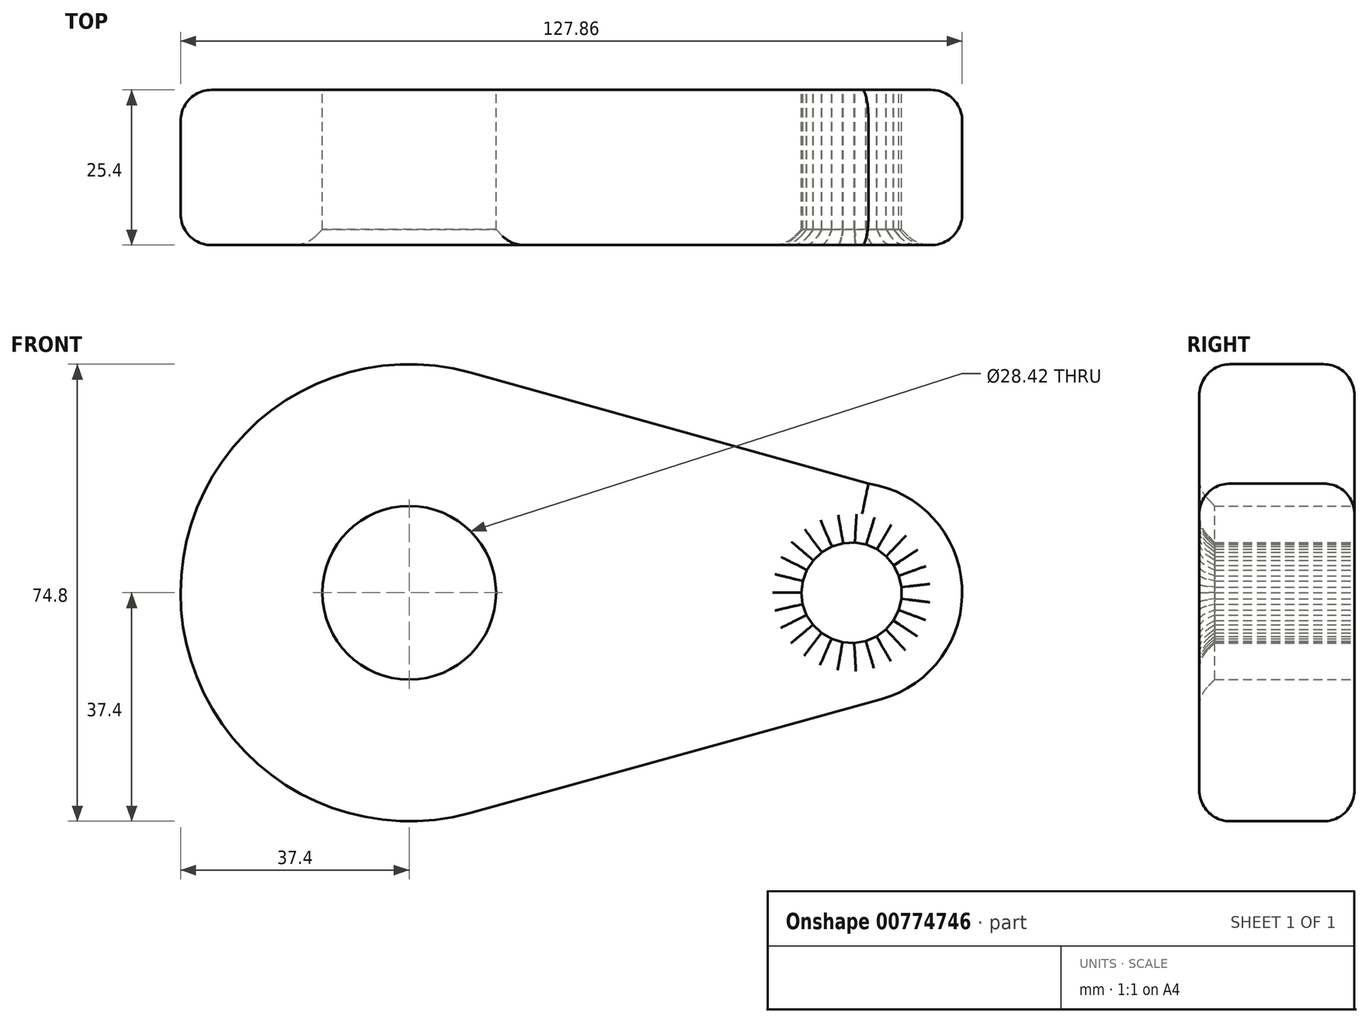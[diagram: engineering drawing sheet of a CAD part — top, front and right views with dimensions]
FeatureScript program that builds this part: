
annotation { "Feature Type Name" : "Feature", "Feature Type Description" : "" }
export const myFeature = defineFeature(function(context is Context, id is Id, definition is map)
    precondition{}
    {
        {
            var Q0;
            Q0=qCreatedBy(makeId("Front.planeOp"),FACE);
            var sketch = newSketch(context, id + "F0", { "sketchPlane" : qUnion([Q0])});
            skCircle(sketch, "E0", {"center": v(0, 0) * mm, "radius": 37.4 * mm});
            skCircle(sketch, "E1", {"center": v(0, 0) * mm, "radius": 14.2 * mm});
            skCircle(sketch, "E2", {"center": v(72.37, 0) * mm, "radius": 18.1 * mm});
            skCircle(sketch, "E3.cCircle", {"center": v(72.37, 0) * mm, "radius": 8.17 * mm, "construction": true});
            skLineSegment(sketch, "E3.0", {"start": v(67.49, 6.62) * mm, "end": v(69.15, 7.57) * mm});
            skLineSegment(sketch, "E3.1", {"start": v(69.15, 7.57) * mm, "end": v(70.98, 8.1) * mm});
            skLineSegment(sketch, "E3.2", {"start": v(70.98, 8.1) * mm, "end": v(72.89, 8.21) * mm});
            skLineSegment(sketch, "E3.3", {"start": v(72.89, 8.21) * mm, "end": v(74.77, 7.87) * mm});
            skLineSegment(sketch, "E3.4", {"start": v(74.77, 7.87) * mm, "end": v(76.52, 7.1) * mm});
            skLineSegment(sketch, "E3.5", {"start": v(76.52, 7.1) * mm, "end": v(78.04, 5.96) * mm});
            skLineSegment(sketch, "E3.6", {"start": v(78.04, 5.96) * mm, "end": v(79.26, 4.5) * mm});
            skLineSegment(sketch, "E3.7", {"start": v(79.26, 4.5) * mm, "end": v(80.11, 2.78) * mm});
            skLineSegment(sketch, "E3.8", {"start": v(80.11, 2.78) * mm, "end": v(80.55, 0.92) * mm});
            skLineSegment(sketch, "E3.9", {"start": v(80.55, 0.92) * mm, "end": v(80.54, -1) * mm});
            skLineSegment(sketch, "E3.10", {"start": v(80.54, -1) * mm, "end": v(80.09, -2.85) * mm});
            skLineSegment(sketch, "E3.11", {"start": v(80.09, -2.85) * mm, "end": v(79.22, -4.55) * mm});
            skLineSegment(sketch, "E3.12", {"start": v(79.22, -4.55) * mm, "end": v(78, -6) * mm});
            skLineSegment(sketch, "E3.13", {"start": v(78, -6) * mm, "end": v(76.45, -7.14) * mm});
            skLineSegment(sketch, "E3.14", {"start": v(76.45, -7.14) * mm, "end": v(74.7, -7.9) * mm});
            skLineSegment(sketch, "E3.15", {"start": v(74.7, -7.9) * mm, "end": v(72.81, -8.22) * mm});
            skLineSegment(sketch, "E3.16", {"start": v(72.81, -8.22) * mm, "end": v(70.9, -8.1) * mm});
            skLineSegment(sketch, "E3.17", {"start": v(70.9, -8.1) * mm, "end": v(69.08, -7.54) * mm});
            skLineSegment(sketch, "E3.18", {"start": v(69.08, -7.54) * mm, "end": v(67.43, -6.58) * mm});
            skLineSegment(sketch, "E3.19", {"start": v(67.43, -6.58) * mm, "end": v(66.04, -5.26) * mm});
            skLineSegment(sketch, "E3.20", {"start": v(66.04, -5.26) * mm, "end": v(65, -3.66) * mm});
            skLineSegment(sketch, "E3.21", {"start": v(65, -3.66) * mm, "end": v(64.36, -1.86) * mm});
            skLineSegment(sketch, "E3.22", {"start": v(64.36, -1.86) * mm, "end": v(64.14, 0.04) * mm});
            skLineSegment(sketch, "E3.23", {"start": v(64.14, 0.04) * mm, "end": v(64.37, 1.93) * mm});
            skLineSegment(sketch, "E3.24", {"start": v(64.37, 1.93) * mm, "end": v(65.03, 3.73) * mm});
            skLineSegment(sketch, "E3.25", {"start": v(65.03, 3.73) * mm, "end": v(66.1, 5.32) * mm});
            skLineSegment(sketch, "E3.26", {"start": v(66.1, 5.32) * mm, "end": v(67.49, 6.62) * mm});
            skPoint(sketch, "E3.0.midPoint", {"position": v(68.32, 7.1) * mm});
            skLineSegment(sketch, "E4", {"start": v(10.04, 36.02) * mm, "end": v(75.13, 17.88) * mm});
            skLineSegment(sketch, "E5", {"start": v(77.2, -17.44) * mm, "end": v(9.98, -36.04) * mm});
            skSolve(sketch);
        }
        {
            var Q0;
            Q0 = qSketchRegion(id + "F0", true);
            extrude(context, id + "F1", {"entities" : qUnion([Q0]), "depth" : 25.4 * mm, "offsetDistance" : 25.4 * mm});
        }
        {
            var Q0;
            Q0=makeQuery(id+"F1.opExtrude","CAP_EDGE",EDGE,{"disambiguationData":[OSD([sQuery(id+"F0.wireOp",EDGE,"E1")])],"isStart":false});
            var Q1;
            Q1=makeQuery(id+"F1.opExtrude","CAP_EDGE",EDGE,{"disambiguationData":[OSD([sQuery(id+"F0.wireOp",EDGE,"E3.4")])],"isStart":false});
            var Q2;
            Q2=makeQuery(id+"F1.opExtrude","CAP_EDGE",EDGE,{"disambiguationData":[OSD([sQuery(id+"F0.wireOp",EDGE,"E3.12")])],"isStart":false});
            var Q3;
            Q3=makeQuery(id+"F1.opExtrude","CAP_EDGE",EDGE,{"disambiguationData":[OSD([sQuery(id+"F0.wireOp",EDGE,"E3.20")])],"isStart":false});
            var Q4;
            Q4=makeQuery(id+"F1.opExtrude","CAP_EDGE",EDGE,{"disambiguationData":[OSD([sQuery(id+"F0.wireOp",EDGE,"E3.5")])],"isStart":false});
            var Q5;
            Q5=makeQuery(id+"F1.opExtrude","CAP_EDGE",EDGE,{"disambiguationData":[OSD([sQuery(id+"F0.wireOp",EDGE,"E3.13")])],"isStart":false});
            var Q6;
            Q6=makeQuery(id+"F1.opExtrude","CAP_EDGE",EDGE,{"disambiguationData":[OSD([sQuery(id+"F0.wireOp",EDGE,"E3.21")])],"isStart":false});
            var Q7;
            Q7=makeQuery(id+"F1.opExtrude","CAP_EDGE",EDGE,{"disambiguationData":[OSD([sQuery(id+"F0.wireOp",EDGE,"E3.6")])],"isStart":false});
            var Q8;
            Q8=makeQuery(id+"F1.opExtrude","CAP_EDGE",EDGE,{"disambiguationData":[OSD([sQuery(id+"F0.wireOp",EDGE,"E3.14")])],"isStart":false});
            var Q9;
            Q9=makeQuery(id+"F1.opExtrude","CAP_EDGE",EDGE,{"disambiguationData":[OSD([sQuery(id+"F0.wireOp",EDGE,"E3.22")])],"isStart":false});
            var Q10;
            Q10=makeQuery(id+"F1.opExtrude","CAP_EDGE",EDGE,{"disambiguationData":[OSD([sQuery(id+"F0.wireOp",EDGE,"E3.7")])],"isStart":false});
            var Q11;
            Q11=makeQuery(id+"F1.opExtrude","CAP_EDGE",EDGE,{"disambiguationData":[OSD([sQuery(id+"F0.wireOp",EDGE,"E3.15")])],"isStart":false});
            var Q12;
            Q12=makeQuery(id+"F1.opExtrude","CAP_EDGE",EDGE,{"disambiguationData":[OSD([sQuery(id+"F0.wireOp",EDGE,"E3.23")])],"isStart":false});
            var Q13;
            Q13=makeQuery(id+"F1.opExtrude","CAP_EDGE",EDGE,{"disambiguationData":[OSD([sQuery(id+"F0.wireOp",EDGE,"E3.0")])],"isStart":false});
            var Q14;
            Q14=makeQuery(id+"F1.opExtrude","CAP_EDGE",EDGE,{"disambiguationData":[OSD([sQuery(id+"F0.wireOp",EDGE,"E3.8")])],"isStart":false});
            var Q15;
            Q15=makeQuery(id+"F1.opExtrude","CAP_EDGE",EDGE,{"disambiguationData":[OSD([sQuery(id+"F0.wireOp",EDGE,"E3.16")])],"isStart":false});
            var Q16;
            Q16=makeQuery(id+"F1.opExtrude","CAP_EDGE",EDGE,{"disambiguationData":[OSD([sQuery(id+"F0.wireOp",EDGE,"E3.24")])],"isStart":false});
            var Q17;
            Q17=makeQuery(id+"F1.opExtrude","CAP_EDGE",EDGE,{"disambiguationData":[OSD([sQuery(id+"F0.wireOp",EDGE,"E3.1")])],"isStart":false});
            var Q18;
            Q18=makeQuery(id+"F1.opExtrude","CAP_EDGE",EDGE,{"disambiguationData":[OSD([sQuery(id+"F0.wireOp",EDGE,"E3.9")])],"isStart":false});
            var Q19;
            Q19=makeQuery(id+"F1.opExtrude","CAP_EDGE",EDGE,{"disambiguationData":[OSD([sQuery(id+"F0.wireOp",EDGE,"E3.17")])],"isStart":false});
            var Q20;
            Q20=makeQuery(id+"F1.opExtrude","CAP_EDGE",EDGE,{"disambiguationData":[OSD([sQuery(id+"F0.wireOp",EDGE,"E3.25")])],"isStart":false});
            var Q21;
            Q21=makeQuery(id+"F1.opExtrude","CAP_EDGE",EDGE,{"disambiguationData":[OSD([sQuery(id+"F0.wireOp",EDGE,"E3.2")])],"isStart":false});
            var Q22;
            Q22=makeQuery(id+"F1.opExtrude","CAP_EDGE",EDGE,{"disambiguationData":[OSD([sQuery(id+"F0.wireOp",EDGE,"E3.10")])],"isStart":false});
            var Q23;
            Q23=makeQuery(id+"F1.opExtrude","CAP_EDGE",EDGE,{"disambiguationData":[OSD([sQuery(id+"F0.wireOp",EDGE,"E3.18")])],"isStart":false});
            var Q24;
            Q24=makeQuery(id+"F1.opExtrude","CAP_EDGE",EDGE,{"disambiguationData":[OSD([sQuery(id+"F0.wireOp",EDGE,"E3.26")])],"isStart":false});
            var Q25;
            Q25=makeQuery(id+"F1.opExtrude","CAP_EDGE",EDGE,{"disambiguationData":[OSD([sQuery(id+"F0.wireOp",EDGE,"E3.3")])],"isStart":false});
            var Q26;
            Q26=makeQuery(id+"F1.opExtrude","CAP_EDGE",EDGE,{"disambiguationData":[OSD([sQuery(id+"F0.wireOp",EDGE,"E3.19")])],"isStart":false});
            var Q27;
            Q27=makeQuery(id+"F1.opExtrude","CAP_EDGE",EDGE,{"disambiguationData":[OSD([sQuery(id+"F0.wireOp",EDGE,"E3.11")])],"isStart":false});
            chamfer(context, id + "F2", {"entities" : qUnion([Q0, Q1, Q2, Q3, Q4, Q5, Q6, Q7, Q8, Q9, Q10, Q11, Q12, Q13, Q14, Q15, Q16, Q17, Q18, Q19, Q20, Q21, Q22, Q23, Q24, Q25, Q26, Q27]), "width" : 2.54 * mm, "tangentPropagation" : true});
        }
        {
            var Q0;
            Q0=makeQuery(id+"F1.opExtrude","CAP_FACE",FACE,{"disambiguationData":[OSD([sQuery(id+"F0.wireOp",EDGE,"E0"),sQuery(id+"F0.wireOp",EDGE,"E1"),sQuery(id+"F0.wireOp",EDGE,"E2"),sQuery(id+"F0.wireOp",EDGE,"E3.0"),sQuery(id+"F0.wireOp",EDGE,"E3.1"),sQuery(id+"F0.wireOp",EDGE,"E3.2"),sQuery(id+"F0.wireOp",EDGE,"E3.3"),sQuery(id+"F0.wireOp",EDGE,"E3.4"),sQuery(id+"F0.wireOp",EDGE,"E3.5"),sQuery(id+"F0.wireOp",EDGE,"E3.6"),sQuery(id+"F0.wireOp",EDGE,"E3.7"),sQuery(id+"F0.wireOp",EDGE,"E3.8"),sQuery(id+"F0.wireOp",EDGE,"E3.9"),sQuery(id+"F0.wireOp",EDGE,"E3.10"),sQuery(id+"F0.wireOp",EDGE,"E3.11"),sQuery(id+"F0.wireOp",EDGE,"E3.12"),sQuery(id+"F0.wireOp",EDGE,"E3.13"),sQuery(id+"F0.wireOp",EDGE,"E3.14"),sQuery(id+"F0.wireOp",EDGE,"E3.15"),sQuery(id+"F0.wireOp",EDGE,"E3.16"),sQuery(id+"F0.wireOp",EDGE,"E3.17"),sQuery(id+"F0.wireOp",EDGE,"E3.18"),sQuery(id+"F0.wireOp",EDGE,"E3.19"),sQuery(id+"F0.wireOp",EDGE,"E3.20"),sQuery(id+"F0.wireOp",EDGE,"E3.21"),sQuery(id+"F0.wireOp",EDGE,"E3.22"),sQuery(id+"F0.wireOp",EDGE,"E3.23"),sQuery(id+"F0.wireOp",EDGE,"E3.24"),sQuery(id+"F0.wireOp",EDGE,"E3.25"),sQuery(id+"F0.wireOp",EDGE,"E3.26"),sQuery(id+"F0.wireOp",EDGE,"E4"),sQuery(id+"F0.wireOp",EDGE,"E5")])],"isStart":false});
            var Q1;
            Q1=makeQuery(id+"F1.opExtrude","CAP_EDGE",EDGE,{"disambiguationData":[OSD([sQuery(id+"F0.wireOp",EDGE,"E5")])],"isStart":true});
            fillet(context, id + "F3", {"entities" : qUnion([Q0, Q1]), "radius" : 5.08 * mm, "tangentPropagation" : true, "allowEdgeOverflow" : false});
        }
    });
